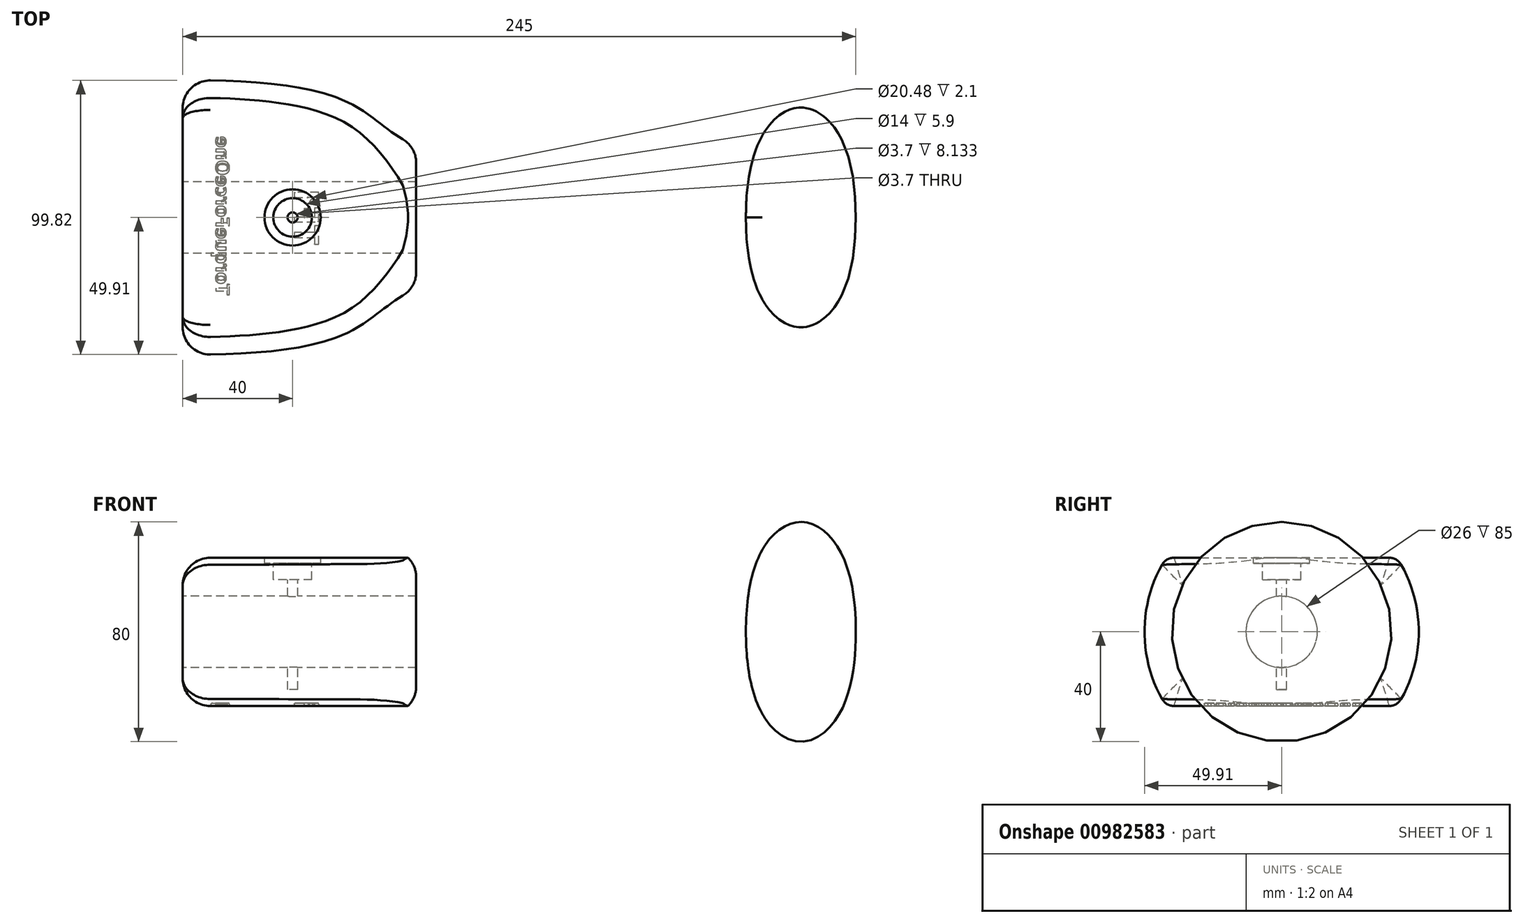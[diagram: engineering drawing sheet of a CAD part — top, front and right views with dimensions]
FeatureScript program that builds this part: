
annotation { "Feature Type Name" : "Feature", "Feature Type Description" : "" }
export const myFeature = defineFeature(function(context is Context, id is Id, definition is map)
    precondition{}
    {
        {
            var Q0;
            Q0=qCreatedBy(makeId("Front.planeOp"),FACE);
            var sketch = newSketch(context, id + "F0", { "sketchPlane" : qUnion([Q0])});
            skLineSegment(sketch, "E0", {"start": v(0, 50) * mm, "end": v(0, 0) * mm});
            skLineSegment(sketch, "E1", {"start": v(0, 0) * mm, "end": v(245, 0) * mm});
            skLineSegment(sketch, "E2", {"start": v(85, 0) * mm, "end": v(85, 26) * mm, "construction": true});
            skLineSegment(sketch, "E3", {"start": v(145, 0) * mm, "end": v(145, 24) * mm, "construction": true});
            skLineSegment(sketch, "E4", {"start": v(205, 0) * mm, "end": v(205, 22) * mm, "construction": true});
            skLineSegment(sketch, "E5", {"start": v(225, 0) * mm, "end": v(225, 40) * mm, "construction": true});
            skLineSegment(sketch, "E6", {"start": v(60, 42) * mm, "end": v(60, 0) * mm, "construction": true});
            skFitSpline(sketch, "E7", {"points": [v(0, 50) * mm, v(60, 42) * mm, v(85, 26) * mm, v(145, 24) * mm, v(205, 22) * mm], "startDerivative": vector(265.83, 0) * mm, "endDerivative": vector(46.66, -3.23) * mm, "construction": true});
            skLineSegment(sketch, "E8", {"start": v(85, 26) * mm, "end": v(85, 0) * mm});
            skLineSegment(sketch, "E9", {"start": v(0, 0) * mm, "end": v(85, 0) * mm});
            skLineSegment(sketch, "E10", {"start": v(205, 22) * mm, "end": v(205, 0) * mm});
            skLineSegment(sketch, "E11", {"start": v(245, 0) * mm, "end": v(205, 0) * mm});
            skLineSegment(sketch, "E12.top", {"start": v(211, 0) * mm, "end": v(239, 0) * mm});
            skFitSpline(sketch, "E13", {"points": [v(196, 22.57) * mm, v(205, 24.2) * mm, v(211.85, 31.36) * mm], "startDerivative": vector(27.96, -1.73) * mm, "endDerivative": vector(11.53, 20.5) * mm});
            skLineSegment(sketch, "E14.bottom", {"start": v(237, 33) * mm, "end": v(213, 33) * mm, "construction": true});
            skLineSegment(sketch, "E14.top", {"start": v(237, -33) * mm, "end": v(213, -33) * mm, "construction": true});
            skLineSegment(sketch, "E14.left", {"start": v(237, 33) * mm, "end": v(237, -33) * mm, "construction": true});
            skLineSegment(sketch, "E14.right", {"start": v(213, 33) * mm, "end": v(213, -33) * mm, "construction": true});
            skPoint(sketch, "E14.middle", {"position": v(225, 0) * mm});
            skLineSegment(sketch, "E15.bottom", {"start": v(239, 0) * mm, "end": v(245, 0) * mm});
            skLineSegment(sketch, "E16.bottom", {"start": v(245, 15) * mm, "end": v(205, 15) * mm, "construction": true});
            skLineSegment(sketch, "E16.top", {"start": v(245, 0) * mm, "end": v(205, 0) * mm, "construction": true});
            skLineSegment(sketch, "E16.right", {"start": v(205, 15) * mm, "end": v(205, 0) * mm, "construction": true});
            skFitSpline(sketch, "E17", {"points": [v(245, 0) * mm, v(237, 33) * mm, v(225, 40) * mm, v(213, 33) * mm, v(205, 0) * mm], "startDerivative": vector(0, 147.57) * mm, "endDerivative": vector(-0.02, -147.57) * mm});
            skFitSpline(sketch, "E18", {"points": [v(0, 50) * mm, v(60, 42) * mm, v(85, 26) * mm, v(145, 23) * mm, v(205, 24) * mm], "startDerivative": vector(265.83, 0) * mm, "endDerivative": vector(46.28, 3.62) * mm});
            skSolve(sketch);
        }
        {
            var Q0;
            {var subQ0=sQuery(id+"F0.wireOp",EDGE,"E0");Q0=makeQuery(id+"F0.imprint","IMPRINT",FACE,{"disambiguationData":[TD([[makeQuery(id+"F0.imprint","IMPRINT",EDGE,{"derivedFrom":subQ0}),1.0]])]});}
            var Q1;
            Q1=makeQuery(id+"F0.imprint","IMPRINT",FACE,{"disambiguationData":[TD([[makeQuery(id+"F0.imprint","IMPRINT",EDGE,{"derivedFrom":sQuery(id+"F0.wireOp",EDGE,"27aa72ab-a35f-4556-a79f-be58b9bce097")}),-1.0]])]});
            var Q2;
            Q2=makeQuery(id+"F0.imprint","IMPRINT",FACE,{"disambiguationData":[TD([[makeQuery(id+"F0.imprint","IMPRINT",EDGE,{"derivedFrom":sQuery(id+"F0.wireOp",EDGE,"E1")}),1.0]])]});
            var Q3;
            {var subQ0=sQuery(id+"F0.wireOp",EDGE,"d97d6b34-898e-417b-85eb-bfbc859b7b58");var subQ4=sQuery(id+"F0.wireOp",EDGE,"E11");var subQ5=makeQuery(id+"F0.imprint","INTERSECT",VERTEX,{"disambiguationData":[OD(0.0)],"derivedFrom":[subQ4,subQ0]});Q3=makeQuery(id+"F0.imprint","IMPRINT",FACE,{"disambiguationData":[TD([[makeQuery(id+"F0.imprint","IMPRINT",EDGE,{"disambiguationData":[TD([[subQ5,-1.0]])],"derivedFrom":subQ4}),-1.0]])]});}
            var Q4;
            {var subQ0=sQuery(id+"F0.wireOp",EDGE,"E10");Q4=makeQuery(id+"F0.imprint","IMPRINT",FACE,{"disambiguationData":[TD([[makeQuery(id+"F0.imprint","IMPRINT",EDGE,{"derivedFrom":subQ0}),1.0]])]});}
            var Q5;
            Q5=sQuery(id+"F0.wireOp",EDGE,"E1");
            revolve(context, id + "F1", {"surfaceOperationType" : NewSurfaceOperationType.NEW, "entities" : qUnion([Q0, Q1, Q2, Q3, Q4]), "axis" : qUnion([Q5]), "revolveType" : RevolveType.FULL});
        }
        {
            var Q0;
            Q0=qCreatedBy(makeId("Right.planeOp"),FACE);
            cPlane(context, id + "F2", {"entities" : qUnion([Q0]), "cplaneType" : CPlaneType.OFFSET, "offset" : 90 * mm, "width" : 150 * mm, "height" : 150 * mm});
        }
        {
            var Q0;
            Q0=qCreatedBy(id+"F2.planeOp",FACE);
            var sketch = newSketch(context, id + "F3", { "sketchPlane" : qUnion([Q0])});
            skLineSegment(sketch, "E19.bottom", {"start": v(-65.87, 27) * mm, "end": v(58.89, 27) * mm});
            skLineSegment(sketch, "E19.top", {"start": v(-65.87, -27) * mm, "end": v(58.89, -27) * mm});
            skLineSegment(sketch, "E19.left", {"start": v(-65.87, 27) * mm, "end": v(-65.87, -27) * mm});
            skLineSegment(sketch, "E19.right", {"start": v(58.89, 27) * mm, "end": v(58.89, -27) * mm});
            skPoint(sketch, "E19.middle", {"position": v(-3.5, 0) * mm});
            skLineSegment(sketch, "E20.bottom", {"start": v(-135.82, 62.52) * mm, "end": v(135.82, 62.52) * mm});
            skLineSegment(sketch, "E20.top", {"start": v(-135.82, -80.38) * mm, "end": v(135.82, -80.38) * mm});
            skLineSegment(sketch, "E20.left", {"start": v(-135.82, 62.52) * mm, "end": v(-135.82, -80.38) * mm});
            skLineSegment(sketch, "E20.right", {"start": v(135.82, 62.52) * mm, "end": v(135.82, -80.38) * mm});
            skPoint(sketch, "E20.middle", {"position": v(0, -8.93) * mm});
            skSolve(sketch);
        }
        {
            var Q0;
            Q0=makeQuery(id+"F3.imprint","IMPRINT",FACE,{"disambiguationData":[TD([[makeQuery(id+"F3.imprint","IMPRINT",EDGE,{"derivedFrom":sQuery(id+"F3.wireOp",EDGE,"E19.bottom")}),1.0]])]});
            extrude(context, id + "F4", {"entities" : qUnion([Q0]), "operationType" : NewBodyOperationType.REMOVE, "oppositeDirection" : true, "depth" : 139 * mm, "offsetDistance" : 25 * mm});
        }
        {
            var Q0;
            Q0=makeQuery(id+"F4.boolean.opBoolean","INTERSECT",EDGE,{"derivedFrom":[makeQuery(id+"F1.opRevolve","SWEPT_FACE",FACE,{"disambiguationData":[OSD([sQuery(id+"F0.wireOp",EDGE,"E18")])]}),makeQuery(id+"F4.opExtrude","SWEPT_FACE",FACE,{"disambiguationData":[OSD([sQuery(id+"F3.wireOp",EDGE,"E19.top")])]})]});
            var Q1;
            Q1=makeQuery(id+"F4.boolean.opBoolean","INTERSECT",EDGE,{"derivedFrom":[makeQuery(id+"F1.opRevolve","SWEPT_FACE",FACE,{"disambiguationData":[OSD([sQuery(id+"F0.wireOp",EDGE,"E18")])]}),makeQuery(id+"F4.opExtrude","SWEPT_FACE",FACE,{"disambiguationData":[OSD([sQuery(id+"F3.wireOp",EDGE,"E19.bottom")])]})]});
            fillet(context, id + "F5", {"entities" : qUnion([Q0, Q1]), "radius" : 5 * mm, "tangentPropagation" : true, "allowEdgeOverflow" : false});
        }
        {
            var Q0;
            {var subQ1=sQuery(id+"F3.wireOp",EDGE,"E19.top");Q0=makeQuery(id+"F7bkeH8S5AFj9gl_1.boolean.opBoolean","SPLIT",FACE,{"disambiguationData":[TD([makeQuery(id+"F4.boolean.opBoolean","COPY",FACE,{"derivedFrom":makeQuery(id+"F4.opExtrude","SWEPT_FACE",FACE,{"disambiguationData":[OSD([subQ1])]})})])],"derivedFrom":makeQuery(id+"F1.opRevolve","SWEPT_FACE",FACE,{"disambiguationData":[OSD([sQuery(id+"F0.wireOp",EDGE,"E0")])]})});}
            var sketch = newSketch(context, id + "F6", { "sketchPlane" : qUnion([Q0])});
            skCircle(sketch, "E21", {"center": v(0, 0) * mm, "radius": 13 * mm});
            skSolve(sketch);
        }
        {
            var Q0;
            Q0=qSketchRegion(id+"F6",true);
            extrude(context, id + "F7", {"entities" : qUnion([Q0]), "operationType" : NewBodyOperationType.REMOVE, "oppositeDirection" : true, "depth" : 100 * mm, "offsetDistance" : 25 * mm});
        }
        {
            var Q0;
            Q0=makeQuery(id+"F4.boolean.opBoolean","COPY",FACE,{"derivedFrom":makeQuery(id+"F4.opExtrude","SWEPT_FACE",FACE,{"disambiguationData":[OSD([sQuery(id+"F3.wireOp",EDGE,"E19.bottom")])]})});
            var sketch = newSketch(context, id + "F8", { "sketchPlane" : qUnion([Q0])});
            skLineSegment(sketch, "E22", {"start": v(0, 0) * mm, "end": v(40, 0) * mm, "construction": true});
            skCircle(sketch, "E23", {"center": v(40, 0) * mm, "radius": 7 * mm});
            skSolve(sketch);
        }
        {
            var Q0;
            Q0 = qSketchRegion(id + "F8", true);
            extrude(context, id + "F9", {"entities" : qUnion([Q0]), "operationType" : NewBodyOperationType.REMOVE, "oppositeDirection" : true, "depth" : 8 * mm, "offsetDistance" : 25 * mm});
        }
        {
            var Q0;
            Q0=makeQuery(id+"F4.boolean.opBoolean","COPY",FACE,{"derivedFrom":makeQuery(id+"F4.opExtrude","SWEPT_FACE",FACE,{"disambiguationData":[OSD([sQuery(id+"F3.wireOp",EDGE,"E19.bottom")])]})});
            var sketch = newSketch(context, id + "F10", { "sketchPlane" : qUnion([Q0])});
            skCircle(sketch, "E24", {"center": v(40, 0) * mm, "radius": 10.24 * mm});
            skCircle(sketch, "E25.0", {"center": v(40, 0) * mm, "radius": 7 * mm});
            skSolve(sketch);
        }
        {
            var Q0;
            Q0 = qSketchRegion(id + "F10", true);
            extrude(context, id + "F11", {"entities" : qUnion([Q0]), "operationType" : NewBodyOperationType.REMOVE, "oppositeDirection" : true, "depth" : 2.1 * mm, "offsetDistance" : 25 * mm});
        }
        {
            var Q0;
            Q0=makeQuery(id+"F9.boolean.opBoolean","COPY",FACE,{"derivedFrom":makeQuery(id+"F9.opExtrude","CAP_FACE",FACE,{"disambiguationData":[OSD([sQuery(id+"F8.wireOp",EDGE,"E23")])],"isStart":false})});
            var sketch = newSketch(context, id + "F12", { "sketchPlane" : qUnion([Q0])});
            skCircle(sketch, "E26", {"center": v(40, 0) * mm, "radius": 1.85 * mm});
            skSolve(sketch);
        }
        {
            var Q0;
            Q0 = qSketchRegion(id + "F12", true);
            extrude(context, id + "F13", {"entities" : qUnion([Q0]), "operationType" : NewBodyOperationType.REMOVE, "oppositeDirection" : true, "depth" : 40 * mm, "offsetDistance" : 25 * mm});
        }
        {
            var Q0;
            Q0=makeQuery(id+"F4.boolean.opBoolean","COPY",FACE,{"derivedFrom":makeQuery(id+"F4.opExtrude","SWEPT_FACE",FACE,{"disambiguationData":[OSD([sQuery(id+"F3.wireOp",EDGE,"E19.top")])]})});
            var sketch = newSketch(context, id + "F14", { "sketchPlane" : qUnion([Q0])});
            skLineSegment(sketch, "E27", {"start": v(0, -0.68) * mm, "end": v(13.52, -0.68) * mm, "construction": true});
            skLineSegment(sketch, "E28.bottom", {"start": v(18.52, -30.68) * mm, "end": v(8.52, -30.68) * mm, "construction": true});
            skLineSegment(sketch, "E28.top", {"start": v(18.52, 29.32) * mm, "end": v(8.52, 29.32) * mm, "construction": true});
            skLineSegment(sketch, "E28.left", {"start": v(18.52, -30.68) * mm, "end": v(18.52, 29.32) * mm, "construction": true});
            skLineSegment(sketch, "E28.right", {"start": v(8.52, -30.68) * mm, "end": v(8.52, 29.32) * mm, "construction": true});
            skPoint(sketch, "E28.middle", {"position": v(13.52, -0.68) * mm});
            skText(sketch, "E29", { "text": "TorqueForceOne", "fontName": "OpenSans-Bold.ttf"});
            const initialGuessF14  = {"E29": [0.012, 0.02832, 0, -1, 0.00502]};
            skSetInitialGuess(sketch, initialGuessF14);
            skSolve(sketch);
        }
        {
            var Q0;
            Q0 = qSketchRegion(id + "F14", true);
            extrude(context, id + "F15", {"entities" : qUnion([Q0]), "operationType" : NewBodyOperationType.REMOVE, "oppositeDirection" : true, "depth" : 1 * mm, "offsetDistance" : 25 * mm});
        }
        {
            var Q0;
            Q0=makeQuery(id+"F15.boolean.opBoolean","COPY",FACE,{"derivedFrom":makeQuery(id+"F15.opExtrude","CAP_FACE",FACE,{"disambiguationData":[OSD([sQuery(id+"F14.wireOp",EDGE,"E29.sketch_text.stroke-0"),sQuery(id+"F14.wireOp",EDGE,"E29.sketch_text.stroke-1"),sQuery(id+"F14.wireOp",EDGE,"E29.sketch_text.stroke-2"),sQuery(id+"F14.wireOp",EDGE,"E29.sketch_text.stroke-3"),sQuery(id+"F14.wireOp",EDGE,"E29.sketch_text.stroke-4"),sQuery(id+"F14.wireOp",EDGE,"E29.sketch_text.stroke-5"),sQuery(id+"F14.wireOp",EDGE,"E29.sketch_text.stroke-6"),sQuery(id+"F14.wireOp",EDGE,"E29.sketch_text.stroke-7")])],"isStart":false})});
            var Q1;
            Q1=makeQuery(id+"F15.boolean.opBoolean","COPY",FACE,{"derivedFrom":makeQuery(id+"F15.opExtrude","CAP_FACE",FACE,{"disambiguationData":[OSD([sQuery(id+"F14.wireOp",EDGE,"E29.sketch_text.stroke-8"),sQuery(id+"F14.wireOp",EDGE,"E29.sketch_text.stroke-9"),sQuery(id+"F14.wireOp",EDGE,"E29.sketch_text.stroke-10"),sQuery(id+"F14.wireOp",EDGE,"E29.sketch_text.stroke-11"),sQuery(id+"F14.wireOp",EDGE,"E29.sketch_text.stroke-12"),sQuery(id+"F14.wireOp",EDGE,"E29.sketch_text.stroke-13"),sQuery(id+"F14.wireOp",EDGE,"E29.sketch_text.stroke-14"),sQuery(id+"F14.wireOp",EDGE,"E29.sketch_text.stroke-15"),sQuery(id+"F14.wireOp",EDGE,"E29.sketch_text.stroke-16"),sQuery(id+"F14.wireOp",EDGE,"E29.sketch_text.stroke-17"),sQuery(id+"F14.wireOp",EDGE,"E29.sketch_text.stroke-18"),sQuery(id+"F14.wireOp",EDGE,"E29.sketch_text.stroke-19"),sQuery(id+"F14.wireOp",EDGE,"E29.sketch_text.stroke-20"),sQuery(id+"F14.wireOp",EDGE,"E29.sketch_text.stroke-21"),sQuery(id+"F14.wireOp",EDGE,"E29.sketch_text.stroke-22"),sQuery(id+"F14.wireOp",EDGE,"E29.sketch_text.stroke-23"),sQuery(id+"F14.wireOp",EDGE,"E29.sketch_text.stroke-24"),sQuery(id+"F14.wireOp",EDGE,"E29.sketch_text.stroke-25")])],"isStart":false})});
            var Q2;
            Q2=makeQuery(id+"F15.boolean.opBoolean","COPY",FACE,{"derivedFrom":makeQuery(id+"F15.opExtrude","CAP_FACE",FACE,{"disambiguationData":[OSD([sQuery(id+"F14.wireOp",EDGE,"E29.sketch_text.stroke-26"),sQuery(id+"F14.wireOp",EDGE,"E29.sketch_text.stroke-27"),sQuery(id+"F14.wireOp",EDGE,"E29.sketch_text.stroke-28"),sQuery(id+"F14.wireOp",EDGE,"E29.sketch_text.stroke-29"),sQuery(id+"F14.wireOp",EDGE,"E29.sketch_text.stroke-30"),sQuery(id+"F14.wireOp",EDGE,"E29.sketch_text.stroke-31"),sQuery(id+"F14.wireOp",EDGE,"E29.sketch_text.stroke-32"),sQuery(id+"F14.wireOp",EDGE,"E29.sketch_text.stroke-33"),sQuery(id+"F14.wireOp",EDGE,"E29.sketch_text.stroke-34"),sQuery(id+"F14.wireOp",EDGE,"E29.sketch_text.stroke-35"),sQuery(id+"F14.wireOp",EDGE,"E29.sketch_text.stroke-36"),sQuery(id+"F14.wireOp",EDGE,"E29.sketch_text.stroke-37"),sQuery(id+"F14.wireOp",EDGE,"E29.sketch_text.stroke-38")])],"isStart":false})});
            var Q3;
            Q3=makeQuery(id+"F15.boolean.opBoolean","COPY",FACE,{"derivedFrom":makeQuery(id+"F15.opExtrude","CAP_FACE",FACE,{"disambiguationData":[OSD([sQuery(id+"F14.wireOp",EDGE,"E29.sketch_text.stroke-39"),sQuery(id+"F14.wireOp",EDGE,"E29.sketch_text.stroke-40"),sQuery(id+"F14.wireOp",EDGE,"E29.sketch_text.stroke-41"),sQuery(id+"F14.wireOp",EDGE,"E29.sketch_text.stroke-42"),sQuery(id+"F14.wireOp",EDGE,"E29.sketch_text.stroke-43"),sQuery(id+"F14.wireOp",EDGE,"E29.sketch_text.stroke-44"),sQuery(id+"F14.wireOp",EDGE,"E29.sketch_text.stroke-45"),sQuery(id+"F14.wireOp",EDGE,"E29.sketch_text.stroke-46"),sQuery(id+"F14.wireOp",EDGE,"E29.sketch_text.stroke-47"),sQuery(id+"F14.wireOp",EDGE,"E29.sketch_text.stroke-48"),sQuery(id+"F14.wireOp",EDGE,"E29.sketch_text.stroke-49"),sQuery(id+"F14.wireOp",EDGE,"E29.sketch_text.stroke-50"),sQuery(id+"F14.wireOp",EDGE,"E29.sketch_text.stroke-51"),sQuery(id+"F14.wireOp",EDGE,"E29.sketch_text.stroke-52"),sQuery(id+"F14.wireOp",EDGE,"E29.sketch_text.stroke-53"),sQuery(id+"F14.wireOp",EDGE,"E29.sketch_text.stroke-54"),sQuery(id+"F14.wireOp",EDGE,"E29.sketch_text.stroke-55"),sQuery(id+"F14.wireOp",EDGE,"E29.sketch_text.stroke-56"),sQuery(id+"F14.wireOp",EDGE,"E29.sketch_text.stroke-57"),sQuery(id+"F14.wireOp",EDGE,"E29.sketch_text.stroke-58"),sQuery(id+"F14.wireOp",EDGE,"E29.sketch_text.stroke-59"),sQuery(id+"F14.wireOp",EDGE,"E29.sketch_text.stroke-60"),sQuery(id+"F14.wireOp",EDGE,"E29.sketch_text.stroke-61"),sQuery(id+"F14.wireOp",EDGE,"E29.sketch_text.stroke-62")])],"isStart":false})});
            var Q4;
            Q4=makeQuery(id+"F15.boolean.opBoolean","COPY",FACE,{"derivedFrom":makeQuery(id+"F15.opExtrude","CAP_FACE",FACE,{"disambiguationData":[OSD([sQuery(id+"F14.wireOp",EDGE,"E29.sketch_text.stroke-63"),sQuery(id+"F14.wireOp",EDGE,"E29.sketch_text.stroke-64"),sQuery(id+"F14.wireOp",EDGE,"E29.sketch_text.stroke-65"),sQuery(id+"F14.wireOp",EDGE,"E29.sketch_text.stroke-66"),sQuery(id+"F14.wireOp",EDGE,"E29.sketch_text.stroke-67"),sQuery(id+"F14.wireOp",EDGE,"E29.sketch_text.stroke-68"),sQuery(id+"F14.wireOp",EDGE,"E29.sketch_text.stroke-69"),sQuery(id+"F14.wireOp",EDGE,"E29.sketch_text.stroke-70"),sQuery(id+"F14.wireOp",EDGE,"E29.sketch_text.stroke-71"),sQuery(id+"F14.wireOp",EDGE,"E29.sketch_text.stroke-72"),sQuery(id+"F14.wireOp",EDGE,"E29.sketch_text.stroke-73"),sQuery(id+"F14.wireOp",EDGE,"E29.sketch_text.stroke-74"),sQuery(id+"F14.wireOp",EDGE,"E29.sketch_text.stroke-75"),sQuery(id+"F14.wireOp",EDGE,"E29.sketch_text.stroke-76"),sQuery(id+"F14.wireOp",EDGE,"E29.sketch_text.stroke-77"),sQuery(id+"F14.wireOp",EDGE,"E29.sketch_text.stroke-78"),sQuery(id+"F14.wireOp",EDGE,"E29.sketch_text.stroke-79")])],"isStart":false})});
            var Q5;
            Q5=makeQuery(id+"F15.boolean.opBoolean","COPY",FACE,{"derivedFrom":makeQuery(id+"F15.opExtrude","CAP_FACE",FACE,{"disambiguationData":[OSD([sQuery(id+"F14.wireOp",EDGE,"E29.sketch_text.stroke-80"),sQuery(id+"F14.wireOp",EDGE,"E29.sketch_text.stroke-81"),sQuery(id+"F14.wireOp",EDGE,"E29.sketch_text.stroke-82"),sQuery(id+"F14.wireOp",EDGE,"E29.sketch_text.stroke-83"),sQuery(id+"F14.wireOp",EDGE,"E29.sketch_text.stroke-84"),sQuery(id+"F14.wireOp",EDGE,"E29.sketch_text.stroke-85"),sQuery(id+"F14.wireOp",EDGE,"E29.sketch_text.stroke-86"),sQuery(id+"F14.wireOp",EDGE,"E29.sketch_text.stroke-87"),sQuery(id+"F14.wireOp",EDGE,"E29.sketch_text.stroke-88"),sQuery(id+"F14.wireOp",EDGE,"E29.sketch_text.stroke-89"),sQuery(id+"F14.wireOp",EDGE,"E29.sketch_text.stroke-90"),sQuery(id+"F14.wireOp",EDGE,"E29.sketch_text.stroke-91"),sQuery(id+"F14.wireOp",EDGE,"E29.sketch_text.stroke-92"),sQuery(id+"F14.wireOp",EDGE,"E29.sketch_text.stroke-93"),sQuery(id+"F14.wireOp",EDGE,"E29.sketch_text.stroke-94"),sQuery(id+"F14.wireOp",EDGE,"E29.sketch_text.stroke-95"),sQuery(id+"F14.wireOp",EDGE,"E29.sketch_text.stroke-96"),sQuery(id+"F14.wireOp",EDGE,"E29.sketch_text.stroke-97"),sQuery(id+"F14.wireOp",EDGE,"E29.sketch_text.stroke-98"),sQuery(id+"F14.wireOp",EDGE,"E29.sketch_text.stroke-99")])],"isStart":false})});
            var Q6;
            Q6=makeQuery(id+"F15.boolean.opBoolean","COPY",FACE,{"derivedFrom":makeQuery(id+"F15.opExtrude","CAP_FACE",FACE,{"disambiguationData":[OSD([sQuery(id+"F14.wireOp",EDGE,"E29.sketch_text.stroke-100"),sQuery(id+"F14.wireOp",EDGE,"E29.sketch_text.stroke-101"),sQuery(id+"F14.wireOp",EDGE,"E29.sketch_text.stroke-102"),sQuery(id+"F14.wireOp",EDGE,"E29.sketch_text.stroke-103"),sQuery(id+"F14.wireOp",EDGE,"E29.sketch_text.stroke-104"),sQuery(id+"F14.wireOp",EDGE,"E29.sketch_text.stroke-105"),sQuery(id+"F14.wireOp",EDGE,"E29.sketch_text.stroke-106"),sQuery(id+"F14.wireOp",EDGE,"E29.sketch_text.stroke-107"),sQuery(id+"F14.wireOp",EDGE,"E29.sketch_text.stroke-108"),sQuery(id+"F14.wireOp",EDGE,"E29.sketch_text.stroke-109")])],"isStart":false})});
            var Q7;
            Q7=makeQuery(id+"F15.boolean.opBoolean","COPY",FACE,{"derivedFrom":makeQuery(id+"F15.opExtrude","CAP_FACE",FACE,{"disambiguationData":[OSD([sQuery(id+"F14.wireOp",EDGE,"E29.sketch_text.stroke-110"),sQuery(id+"F14.wireOp",EDGE,"E29.sketch_text.stroke-111"),sQuery(id+"F14.wireOp",EDGE,"E29.sketch_text.stroke-112"),sQuery(id+"F14.wireOp",EDGE,"E29.sketch_text.stroke-113"),sQuery(id+"F14.wireOp",EDGE,"E29.sketch_text.stroke-114"),sQuery(id+"F14.wireOp",EDGE,"E29.sketch_text.stroke-115"),sQuery(id+"F14.wireOp",EDGE,"E29.sketch_text.stroke-116"),sQuery(id+"F14.wireOp",EDGE,"E29.sketch_text.stroke-117"),sQuery(id+"F14.wireOp",EDGE,"E29.sketch_text.stroke-118"),sQuery(id+"F14.wireOp",EDGE,"E29.sketch_text.stroke-119"),sQuery(id+"F14.wireOp",EDGE,"E29.sketch_text.stroke-120"),sQuery(id+"F14.wireOp",EDGE,"E29.sketch_text.stroke-121"),sQuery(id+"F14.wireOp",EDGE,"E29.sketch_text.stroke-122"),sQuery(id+"F14.wireOp",EDGE,"E29.sketch_text.stroke-123"),sQuery(id+"F14.wireOp",EDGE,"E29.sketch_text.stroke-124"),sQuery(id+"F14.wireOp",EDGE,"E29.sketch_text.stroke-125"),sQuery(id+"F14.wireOp",EDGE,"E29.sketch_text.stroke-126"),sQuery(id+"F14.wireOp",EDGE,"E29.sketch_text.stroke-127")])],"isStart":false})});
            var Q8;
            Q8=makeQuery(id+"F15.boolean.opBoolean","COPY",FACE,{"derivedFrom":makeQuery(id+"F15.opExtrude","CAP_FACE",FACE,{"disambiguationData":[OSD([sQuery(id+"F14.wireOp",EDGE,"E29.sketch_text.stroke-128"),sQuery(id+"F14.wireOp",EDGE,"E29.sketch_text.stroke-129"),sQuery(id+"F14.wireOp",EDGE,"E29.sketch_text.stroke-130"),sQuery(id+"F14.wireOp",EDGE,"E29.sketch_text.stroke-131"),sQuery(id+"F14.wireOp",EDGE,"E29.sketch_text.stroke-132"),sQuery(id+"F14.wireOp",EDGE,"E29.sketch_text.stroke-133"),sQuery(id+"F14.wireOp",EDGE,"E29.sketch_text.stroke-134"),sQuery(id+"F14.wireOp",EDGE,"E29.sketch_text.stroke-135"),sQuery(id+"F14.wireOp",EDGE,"E29.sketch_text.stroke-136"),sQuery(id+"F14.wireOp",EDGE,"E29.sketch_text.stroke-137"),sQuery(id+"F14.wireOp",EDGE,"E29.sketch_text.stroke-138"),sQuery(id+"F14.wireOp",EDGE,"E29.sketch_text.stroke-139"),sQuery(id+"F14.wireOp",EDGE,"E29.sketch_text.stroke-140")])],"isStart":false})});
            var Q9;
            Q9=makeQuery(id+"F15.boolean.opBoolean","COPY",FACE,{"derivedFrom":makeQuery(id+"F15.opExtrude","CAP_FACE",FACE,{"disambiguationData":[OSD([sQuery(id+"F14.wireOp",EDGE,"E29.sketch_text.stroke-141"),sQuery(id+"F14.wireOp",EDGE,"E29.sketch_text.stroke-142"),sQuery(id+"F14.wireOp",EDGE,"E29.sketch_text.stroke-143"),sQuery(id+"F14.wireOp",EDGE,"E29.sketch_text.stroke-144"),sQuery(id+"F14.wireOp",EDGE,"E29.sketch_text.stroke-145"),sQuery(id+"F14.wireOp",EDGE,"E29.sketch_text.stroke-146"),sQuery(id+"F14.wireOp",EDGE,"E29.sketch_text.stroke-147"),sQuery(id+"F14.wireOp",EDGE,"E29.sketch_text.stroke-148"),sQuery(id+"F14.wireOp",EDGE,"E29.sketch_text.stroke-149"),sQuery(id+"F14.wireOp",EDGE,"E29.sketch_text.stroke-150"),sQuery(id+"F14.wireOp",EDGE,"E29.sketch_text.stroke-151"),sQuery(id+"F14.wireOp",EDGE,"E29.sketch_text.stroke-152"),sQuery(id+"F14.wireOp",EDGE,"E29.sketch_text.stroke-153"),sQuery(id+"F14.wireOp",EDGE,"E29.sketch_text.stroke-154")])],"isStart":false})});
            var Q10;
            Q10=makeQuery(id+"F15.boolean.opBoolean","COPY",FACE,{"derivedFrom":makeQuery(id+"F15.opExtrude","CAP_FACE",FACE,{"disambiguationData":[OSD([sQuery(id+"F14.wireOp",EDGE,"E29.sketch_text.stroke-155"),sQuery(id+"F14.wireOp",EDGE,"E29.sketch_text.stroke-156"),sQuery(id+"F14.wireOp",EDGE,"E29.sketch_text.stroke-157"),sQuery(id+"F14.wireOp",EDGE,"E29.sketch_text.stroke-158"),sQuery(id+"F14.wireOp",EDGE,"E29.sketch_text.stroke-159"),sQuery(id+"F14.wireOp",EDGE,"E29.sketch_text.stroke-160"),sQuery(id+"F14.wireOp",EDGE,"E29.sketch_text.stroke-161"),sQuery(id+"F14.wireOp",EDGE,"E29.sketch_text.stroke-162"),sQuery(id+"F14.wireOp",EDGE,"E29.sketch_text.stroke-163"),sQuery(id+"F14.wireOp",EDGE,"E29.sketch_text.stroke-164"),sQuery(id+"F14.wireOp",EDGE,"E29.sketch_text.stroke-165"),sQuery(id+"F14.wireOp",EDGE,"E29.sketch_text.stroke-166"),sQuery(id+"F14.wireOp",EDGE,"E29.sketch_text.stroke-167"),sQuery(id+"F14.wireOp",EDGE,"E29.sketch_text.stroke-168"),sQuery(id+"F14.wireOp",EDGE,"E29.sketch_text.stroke-169"),sQuery(id+"F14.wireOp",EDGE,"E29.sketch_text.stroke-170"),sQuery(id+"F14.wireOp",EDGE,"E29.sketch_text.stroke-171"),sQuery(id+"F14.wireOp",EDGE,"E29.sketch_text.stroke-172"),sQuery(id+"F14.wireOp",EDGE,"E29.sketch_text.stroke-173"),sQuery(id+"F14.wireOp",EDGE,"E29.sketch_text.stroke-174")])],"isStart":false})});
            var Q11;
            Q11=makeQuery(id+"F15.boolean.opBoolean","COPY",FACE,{"derivedFrom":makeQuery(id+"F15.opExtrude","CAP_FACE",FACE,{"disambiguationData":[OSD([sQuery(id+"F14.wireOp",EDGE,"E29.sketch_text.stroke-175"),sQuery(id+"F14.wireOp",EDGE,"E29.sketch_text.stroke-176"),sQuery(id+"F14.wireOp",EDGE,"E29.sketch_text.stroke-177"),sQuery(id+"F14.wireOp",EDGE,"E29.sketch_text.stroke-178"),sQuery(id+"F14.wireOp",EDGE,"E29.sketch_text.stroke-179"),sQuery(id+"F14.wireOp",EDGE,"E29.sketch_text.stroke-180"),sQuery(id+"F14.wireOp",EDGE,"E29.sketch_text.stroke-181"),sQuery(id+"F14.wireOp",EDGE,"E29.sketch_text.stroke-182"),sQuery(id+"F14.wireOp",EDGE,"E29.sketch_text.stroke-183"),sQuery(id+"F14.wireOp",EDGE,"E29.sketch_text.stroke-184"),sQuery(id+"F14.wireOp",EDGE,"E29.sketch_text.stroke-185"),sQuery(id+"F14.wireOp",EDGE,"E29.sketch_text.stroke-186"),sQuery(id+"F14.wireOp",EDGE,"E29.sketch_text.stroke-187"),sQuery(id+"F14.wireOp",EDGE,"E29.sketch_text.stroke-188")])],"isStart":false})});
            var Q12;
            Q12=makeQuery(id+"F15.boolean.opBoolean","COPY",FACE,{"derivedFrom":makeQuery(id+"F15.opExtrude","CAP_FACE",FACE,{"disambiguationData":[OSD([sQuery(id+"F14.wireOp",EDGE,"E29.sketch_text.stroke-189"),sQuery(id+"F14.wireOp",EDGE,"E29.sketch_text.stroke-190"),sQuery(id+"F14.wireOp",EDGE,"E29.sketch_text.stroke-191"),sQuery(id+"F14.wireOp",EDGE,"E29.sketch_text.stroke-192"),sQuery(id+"F14.wireOp",EDGE,"E29.sketch_text.stroke-193"),sQuery(id+"F14.wireOp",EDGE,"E29.sketch_text.stroke-194"),sQuery(id+"F14.wireOp",EDGE,"E29.sketch_text.stroke-195"),sQuery(id+"F14.wireOp",EDGE,"E29.sketch_text.stroke-196"),sQuery(id+"F14.wireOp",EDGE,"E29.sketch_text.stroke-197"),sQuery(id+"F14.wireOp",EDGE,"E29.sketch_text.stroke-198"),sQuery(id+"F14.wireOp",EDGE,"E29.sketch_text.stroke-199"),sQuery(id+"F14.wireOp",EDGE,"E29.sketch_text.stroke-200"),sQuery(id+"F14.wireOp",EDGE,"E29.sketch_text.stroke-201"),sQuery(id+"F14.wireOp",EDGE,"E29.sketch_text.stroke-202"),sQuery(id+"F14.wireOp",EDGE,"E29.sketch_text.stroke-203"),sQuery(id+"F14.wireOp",EDGE,"E29.sketch_text.stroke-204"),sQuery(id+"F14.wireOp",EDGE,"E29.sketch_text.stroke-205")])],"isStart":false})});
            var Q13;
            Q13=makeQuery(id+"F15.boolean.opBoolean","COPY",FACE,{"derivedFrom":makeQuery(id+"F15.opExtrude","CAP_FACE",FACE,{"disambiguationData":[OSD([sQuery(id+"F14.wireOp",EDGE,"E29.sketch_text.stroke-206"),sQuery(id+"F14.wireOp",EDGE,"E29.sketch_text.stroke-207"),sQuery(id+"F14.wireOp",EDGE,"E29.sketch_text.stroke-208"),sQuery(id+"F14.wireOp",EDGE,"E29.sketch_text.stroke-209"),sQuery(id+"F14.wireOp",EDGE,"E29.sketch_text.stroke-210"),sQuery(id+"F14.wireOp",EDGE,"E29.sketch_text.stroke-211"),sQuery(id+"F14.wireOp",EDGE,"E29.sketch_text.stroke-212"),sQuery(id+"F14.wireOp",EDGE,"E29.sketch_text.stroke-213"),sQuery(id+"F14.wireOp",EDGE,"E29.sketch_text.stroke-214"),sQuery(id+"F14.wireOp",EDGE,"E29.sketch_text.stroke-215"),sQuery(id+"F14.wireOp",EDGE,"E29.sketch_text.stroke-216"),sQuery(id+"F14.wireOp",EDGE,"E29.sketch_text.stroke-217"),sQuery(id+"F14.wireOp",EDGE,"E29.sketch_text.stroke-218"),sQuery(id+"F14.wireOp",EDGE,"E29.sketch_text.stroke-219"),sQuery(id+"F14.wireOp",EDGE,"E29.sketch_text.stroke-220"),sQuery(id+"F14.wireOp",EDGE,"E29.sketch_text.stroke-221"),sQuery(id+"F14.wireOp",EDGE,"E29.sketch_text.stroke-222"),sQuery(id+"F14.wireOp",EDGE,"E29.sketch_text.stroke-223"),sQuery(id+"F14.wireOp",EDGE,"E29.sketch_text.stroke-224"),sQuery(id+"F14.wireOp",EDGE,"E29.sketch_text.stroke-225")])],"isStart":false})});
            fillet(context, id + "F16", {"entities" : qUnion([Q0, Q1, Q2, Q3, Q4, Q5, Q6, Q7, Q8, Q9, Q10, Q11, Q12, Q13]), "radius" : .3 * mm, "tangentPropagation" : true, "allowEdgeOverflow" : false});
        }
        {
            var Q0;
            {var subQ0=sQuery(id+"F3.wireOp",EDGE,"E19.top");Q0=makeQuery(id+"F15.boolean.opBoolean","SPLIT",FACE,{"disambiguationData":[TD([makeQuery(id+"F1.opRevolve","SWEPT_FACE",FACE,{"disambiguationData":[OSD([sQuery(id+"F0.wireOp",EDGE,"E0")])]})])],"derivedFrom":makeQuery(id+"F4.boolean.opBoolean","COPY",FACE,{"derivedFrom":makeQuery(id+"F4.opExtrude","SWEPT_FACE",FACE,{"disambiguationData":[OSD([subQ0])]})})});}
            var sketch = newSketch(context, id + "F17", { "sketchPlane" : qUnion([Q0])});
            skLineSegment(sketch, "E30", {"start": v(0, 0) * mm, "end": v(45, 0) * mm, "construction": true});
            skLineSegment(sketch, "E31.bottom", {"start": v(49.39, -10) * mm, "end": v(40.61, -10) * mm, "construction": true});
            skLineSegment(sketch, "E31.top", {"start": v(49.39, 10) * mm, "end": v(40.61, 10) * mm, "construction": true});
            skLineSegment(sketch, "E31.left", {"start": v(49.39, -10) * mm, "end": v(49.39, 10) * mm, "construction": true});
            skLineSegment(sketch, "E31.right", {"start": v(40.61, -10) * mm, "end": v(40.61, 10) * mm, "construction": true});
            skPoint(sketch, "E31.middle", {"position": v(45, 0) * mm});
            skText(sketch, "E32", { "text": "TF1", "fontName": "OpenSans-Bold.ttf"});
            const initialGuessF17  = {"E32": [0.04061, 0.01, 0, -1, 0.00897]};
            skSetInitialGuess(sketch, initialGuessF17);
            skSolve(sketch);
        }
        {
            var Q0;
            Q0 = qSketchRegion(id + "F17", true);
            extrude(context, id + "F18", {"entities" : qUnion([Q0]), "operationType" : NewBodyOperationType.REMOVE, "oppositeDirection" : true, "depth" : 1 * mm, "offsetDistance" : 25 * mm});
        }
        {
            var Q0;
            Q0=makeQuery(id+"F18.boolean.opBoolean","COPY",FACE,{"derivedFrom":makeQuery(id+"F18.opExtrude","CAP_FACE",FACE,{"disambiguationData":[OSD([sQuery(id+"F17.wireOp",EDGE,"E32.sketch_text.stroke-0"),sQuery(id+"F17.wireOp",EDGE,"E32.sketch_text.stroke-1"),sQuery(id+"F17.wireOp",EDGE,"E32.sketch_text.stroke-2"),sQuery(id+"F17.wireOp",EDGE,"E32.sketch_text.stroke-3"),sQuery(id+"F17.wireOp",EDGE,"E32.sketch_text.stroke-4"),sQuery(id+"F17.wireOp",EDGE,"E32.sketch_text.stroke-5"),sQuery(id+"F17.wireOp",EDGE,"E32.sketch_text.stroke-6"),sQuery(id+"F17.wireOp",EDGE,"E32.sketch_text.stroke-7")])],"isStart":false})});
            var Q1;
            Q1=makeQuery(id+"F18.boolean.opBoolean","COPY",FACE,{"derivedFrom":makeQuery(id+"F18.opExtrude","CAP_FACE",FACE,{"disambiguationData":[OSD([sQuery(id+"F17.wireOp",EDGE,"E32.sketch_text.stroke-8"),sQuery(id+"F17.wireOp",EDGE,"E32.sketch_text.stroke-9"),sQuery(id+"F17.wireOp",EDGE,"E32.sketch_text.stroke-10"),sQuery(id+"F17.wireOp",EDGE,"E32.sketch_text.stroke-11"),sQuery(id+"F17.wireOp",EDGE,"E32.sketch_text.stroke-12"),sQuery(id+"F17.wireOp",EDGE,"E32.sketch_text.stroke-13"),sQuery(id+"F17.wireOp",EDGE,"E32.sketch_text.stroke-14"),sQuery(id+"F17.wireOp",EDGE,"E32.sketch_text.stroke-15"),sQuery(id+"F17.wireOp",EDGE,"E32.sketch_text.stroke-16"),sQuery(id+"F17.wireOp",EDGE,"E32.sketch_text.stroke-17")])],"isStart":false})});
            var Q2;
            Q2=makeQuery(id+"F18.boolean.opBoolean","COPY",FACE,{"derivedFrom":makeQuery(id+"F18.opExtrude","CAP_FACE",FACE,{"disambiguationData":[OSD([sQuery(id+"F17.wireOp",EDGE,"E32.sketch_text.stroke-18"),sQuery(id+"F17.wireOp",EDGE,"E32.sketch_text.stroke-19"),sQuery(id+"F17.wireOp",EDGE,"E32.sketch_text.stroke-20"),sQuery(id+"F17.wireOp",EDGE,"E32.sketch_text.stroke-21"),sQuery(id+"F17.wireOp",EDGE,"E32.sketch_text.stroke-22"),sQuery(id+"F17.wireOp",EDGE,"E32.sketch_text.stroke-23"),sQuery(id+"F17.wireOp",EDGE,"E32.sketch_text.stroke-24"),sQuery(id+"F17.wireOp",EDGE,"E32.sketch_text.stroke-25"),sQuery(id+"F17.wireOp",EDGE,"E32.sketch_text.stroke-26"),sQuery(id+"F17.wireOp",EDGE,"E32.sketch_text.stroke-27")])],"isStart":false})});
            fillet(context, id + "F19", {"entities" : qUnion([Q0, Q1, Q2]), "radius" : .3 * mm, "tangentPropagation" : true, "allowEdgeOverflow" : false});
        }
        {
            var Q0;
            Q0=makeQuery(id+"F1.opRevolve","SWEPT_EDGE",EDGE,{"disambiguationData":[OSD([sQuery(id+"F0.wireOp",EDGE,"E13"),sQuery(id+"F0.wireOp",EDGE,"E18")])]});
            fillet(context, id + "F20", {"entities" : qUnion([Q0]), "radius" : 10 * mm, "tangentPropagation" : true, "allowEdgeOverflow" : false});
        }
    });
